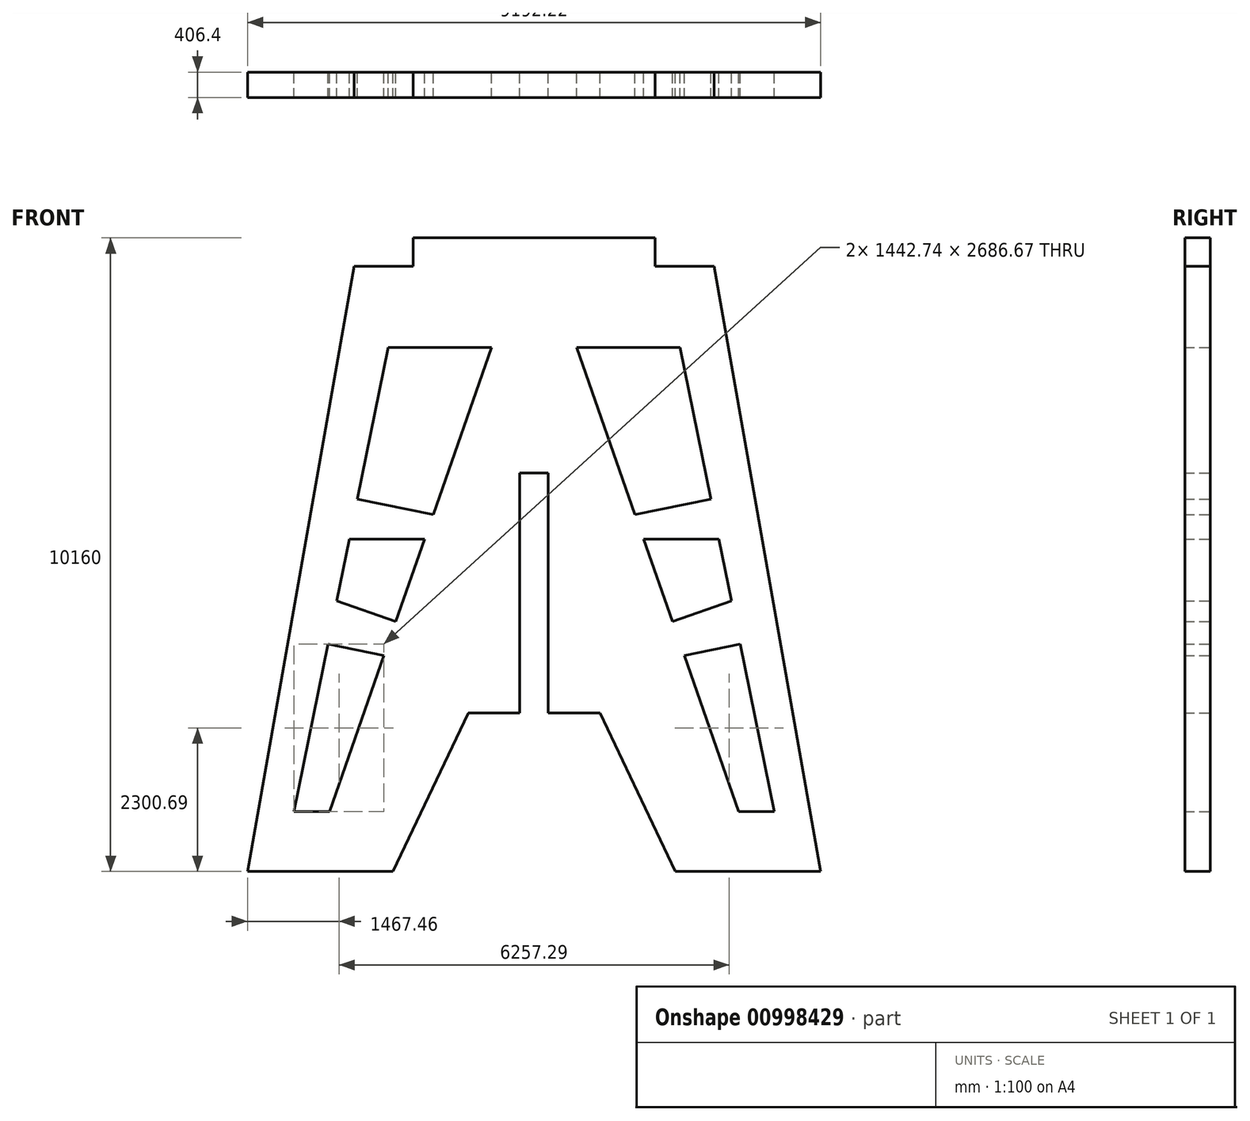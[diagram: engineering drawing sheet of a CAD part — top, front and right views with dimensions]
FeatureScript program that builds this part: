
annotation { "Feature Type Name" : "Feature", "Feature Type Description" : "" }
export const myFeature = defineFeature(function(context is Context, id is Id, definition is map)
    precondition{}
    {
        {
            var Q0;
            Q0=qCreatedBy(makeId("Front.planeOp"),FACE);
            var sketch = newSketch(context, id + "F0", { "sketchPlane" : qUnion([Q0])});
            skLineSegment(sketch, "E0", {"start": v(-10019.31, -2540) * mm, "end": v(-8308.45, 7162.8) * mm});
            skLineSegment(sketch, "E1", {"start": v(-7360.64, 7620) * mm, "end": v(-3485.76, 7620) * mm});
            skLineSegment(sketch, "E2", {"start": v(-2537.96, 7162.8) * mm, "end": v(-827.1, -2540) * mm});
            skLineSegment(sketch, "E3", {"start": v(-827.1, -2540) * mm, "end": v(-3162.33, -2540) * mm});
            skLineSegment(sketch, "E4", {"start": v(-7684.08, -2540) * mm, "end": v(-6479.5, -3.63) * mm});
            skLineSegment(sketch, "E5", {"start": v(-4368.62, 0) * mm, "end": v(-3162.33, -2540) * mm});
            skLineSegment(sketch, "E6.trimOffspring", {"start": v(-7684.08, -2540) * mm, "end": v(-10019.31, -2540) * mm});
            skLineSegment(sketch, "E7", {"start": v(-7360.64, 7620) * mm, "end": v(-7360.64, 7162.8) * mm});
            skLineSegment(sketch, "E8", {"start": v(-7360.64, 7162.8) * mm, "end": v(-8308.45, 7162.8) * mm});
            skLineSegment(sketch, "E9", {"start": v(-3485.76, 7620) * mm, "end": v(-3485.76, 7162.8) * mm});
            skLineSegment(sketch, "E10", {"start": v(-3485.76, 7162.8) * mm, "end": v(-2537.96, 7162.8) * mm});
            skLineSegment(sketch, "E11", {"start": v(-5423.2, 7620) * mm, "end": v(-5423.2, -4451.39) * mm, "construction": true});
            skLineSegment(sketch, "E12.top", {"start": v(-5651.8, 3848.48) * mm, "end": v(-5194.6, 3848.48) * mm});
            skLineSegment(sketch, "E12.left", {"start": v(-5651.8, 0) * mm, "end": v(-5651.8, 3848.48) * mm});
            skLineSegment(sketch, "E12.right", {"start": v(-5194.6, 0) * mm, "end": v(-5194.6, 3848.48) * mm});
            skLineSegment(sketch, "E13", {"start": v(-6473.77, 0) * mm, "end": v(-5651.8, 0) * mm});
            skLineSegment(sketch, "E14", {"start": v(-5194.6, 0) * mm, "end": v(-4368.62, 0) * mm});
            skLineSegment(sketch, "E15", {"start": v(-1573.18, -1582.64) * mm, "end": v(-2117.66, 1104.03) * mm});
            skLineSegment(sketch, "E16", {"start": v(-3082.37, 5864.3) * mm, "end": v(-4740, 5864.3) * mm});
            skLineSegment(sketch, "E17", {"start": v(-4740, 5864.3) * mm, "end": v(-3804.7, 3183.14) * mm});
            skLineSegment(sketch, "E18", {"start": v(-2142.22, -1582.64) * mm, "end": v(-1573.18, -1582.64) * mm});
            skLineSegment(sketch, "E19", {"start": v(-3804.7, 3183.14) * mm, "end": v(-2588.94, 3429.52) * mm});
            skLineSegment(sketch, "E20", {"start": v(-2458.82, 2787.45) * mm, "end": v(-3666.67, 2787.45) * mm});
            skLineSegment(sketch, "E21", {"start": v(-2258.37, 1798.33) * mm, "end": v(-3206.28, 1467.67) * mm});
            skLineSegment(sketch, "E22", {"start": v(-2117.66, 1104.03) * mm, "end": v(-3015.93, 921.98) * mm});
            skLineSegment(sketch, "E23.trimOffspring", {"start": v(-3666.67, 2787.45) * mm, "end": v(-3206.28, 1467.67) * mm});
            skLineSegment(sketch, "E24.trimOffspring", {"start": v(-2588.94, 3429.52) * mm, "end": v(-3082.37, 5864.3) * mm});
            skLineSegment(sketch, "E25.trimOffspring", {"start": v(-2258.37, 1798.33) * mm, "end": v(-2458.82, 2787.45) * mm});
            skLineSegment(sketch, "E26.trimOffspring", {"start": v(-3015.93, 921.98) * mm, "end": v(-2142.22, -1582.64) * mm});
            skLineSegment(sketch, "E27.MirrorCS", {"start": v(-8704.18, -1582.64) * mm, "end": v(-9273.22, -1582.64) * mm});
            skLineSegment(sketch, "E28.MirrorCS", {"start": v(-9273.22, -1582.64) * mm, "end": v(-8728.75, 1104.03) * mm});
            skLineSegment(sketch, "E29.MirrorCS", {"start": v(-8387.59, 2787.45) * mm, "end": v(-7179.73, 2787.45) * mm});
            skLineSegment(sketch, "E30.MirrorCS", {"start": v(-7830.48, 921.98) * mm, "end": v(-8704.18, -1582.64) * mm});
            skLineSegment(sketch, "E31.MirrorCS", {"start": v(-8588.04, 1798.33) * mm, "end": v(-7640.12, 1467.67) * mm});
            skLineSegment(sketch, "E32.MirrorCS", {"start": v(-6106.41, 5864.3) * mm, "end": v(-7041.7, 3183.14) * mm});
            skLineSegment(sketch, "E33.MirrorCS", {"start": v(-7179.73, 2787.45) * mm, "end": v(-7640.12, 1467.67) * mm});
            skLineSegment(sketch, "E34.MirrorCS", {"start": v(-8728.75, 1104.03) * mm, "end": v(-7830.48, 921.98) * mm});
            skLineSegment(sketch, "E35.MirrorCS", {"start": v(-8588.04, 1798.33) * mm, "end": v(-8387.59, 2787.45) * mm});
            skLineSegment(sketch, "E36.MirrorCS", {"start": v(-7041.7, 3183.14) * mm, "end": v(-8257.47, 3429.52) * mm});
            skLineSegment(sketch, "E37.MirrorCS", {"start": v(-7764.04, 5864.3) * mm, "end": v(-6106.41, 5864.3) * mm});
            skLineSegment(sketch, "E38.MirrorCS", {"start": v(-8257.47, 3429.52) * mm, "end": v(-7764.04, 5864.3) * mm});
            skPoint(sketch, "E39.visualSharp", {"position": v(-6477.78, 0) * mm});
            skArc(sketch, "E39.filletArc", {"start": v(-6473.77, 0) * mm, "mid": v(-6477.16, -0.98) * mm, "end": v(-6479.5, -3.63) * mm});
            skSolve(sketch);
        }
        {
            var Q0;
            Q0=makeQuery(id+"F0.imprint","IMPRINT",FACE,{"disambiguationData":[TD([[makeQuery(id+"F0.imprint","IMPRINT",EDGE,{"derivedFrom":sQuery(id+"F0.wireOp",EDGE,"E0")}),-1.0]])]});
            extrude(context, id + "F1", {"entities" : qUnion([Q0]), "depth" : 406.4 * mm, "offsetDistance" : 25.4 * mm});
        }
    });
